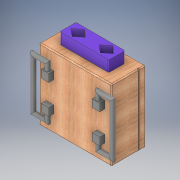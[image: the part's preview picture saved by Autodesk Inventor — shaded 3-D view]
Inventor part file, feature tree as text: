
AUTODESK INVENTOR PART (.ipt)
format: ipt  version: 2018 (Build 220112000, 112)  size: 627,200 bytes
history: native  units: in
note: dims shown in document units (in); Inventor stores cm internally (conversion verified against a paired STEP export)
features: extrude x16, sketch x16, projected_geometry x8, fillet x2
ambient origin geometry x8: Origin, YZ Plane, XZ Plane, XY Plane, X Axis, Y Axis, Z Axis, Center Point
bodies: Solid1 (feature_tree)
feature tree (42):
  extrude  "Extrusion1"  Depth=3.175in
  extrude  "Extrusion2"  Depth=1.517in TaperAngle=0.0deg
  fillet  "Fillet1"  Radius=3.175in
  extrude  "Extrusion3"  Depth=3.23in
  extrude  "Extrusion4"  Depth=0.8225in
  extrude  "Extrusion5"  Depth=0.05in
  extrude  "Extrusion6"  Depth=0.05in
  extrude  "Extrusion7"  Depth=0.31in
  extrude  "Extrusion8"  Depth=0.31in
  fillet  "Fillet2"  Radius=0.76in
  extrude  "Extrusion9"  Depth=0.76in
  extrude  "Extrusion10"  Depth=0.34in
  extrude  "Extrusion11"  Depth=0.34in
  extrude  "Extrusion12"  Depth=0.34in
  extrude  "Extrusion13"  Depth=0.0975in
  extrude  "Extrusion14"  Depth=0.0975in
  extrude  "Extrusion15"  Depth=0.0975in
  extrude  "Extrusion16"  Depth=1.155in
  sketch  "Sketch1"  dims[d0=3.23in d1=3.175in]
  sketch  "Sketch2"  dims[d2=0.05in d3=1.517in d4=0.0in d5=3.175in]
  sketch  "Sketch3"  dims[d8=3.23in d9=0.695in]
  sketch  "Sketch4"  dims[d10=0.8225in d11=0.8225in]
  sketch  "Sketch5"  dims[d12=0.695in d13=0.05in]
  projected_geometry  "Projected Loop1"
  projected_geometry  "Projected Loop2"
  sketch  "Sketch6"  dims[d14=1.155in d15=0.0in d16=0.05in]
  sketch  "Sketch7"  dims[d26=0.31in d27=0.31in]
  projected_geometry  "Projected Loop3"
  projected_geometry  "Projected Loop4"
  sketch  "Sketch8"  dims[d28=0.31in d29=0.31in d30=0.76in]
  sketch  "Sketch9"  dims[d31=0.76in d32=0.76in]
  sketch  "Sketch10"  dims[d33=0.76in d34=0.34in]
  sketch  "Sketch11"  dims[d35=0.34in d36=0.34in]
  sketch  "Sketch12"  dims[d37=0.34in d38=0.34in]
  projected_geometry  "Projected Loop5"
  projected_geometry  "Projected Loop6"
  projected_geometry  "Projected Loop7"
  sketch  "Sketch13"  dims[d39=0.215in d40=0.0in d42=0.0975in]
  sketch  "Sketch14"  dims[d43=0.0975in d44=0.195in]
  sketch  "Sketch15"  dims[d45=0.195in d46=0.0975in]
  projected_geometry  "Projected Loop8"
  sketch  "Sketch16"  dims[d47=0.0975in d48=0.195in d49=0.195in d50=0.3975in d51=0.0in d52=0.3975in d53=0.0in d54=0.195in d55=0.195in d56=0.63in d57=0.0in d58=0.63in d59=0.0in d60=0.195in d61=0.195in d62=0.195in d63=0.195in d64=0.63in d65=0.0in d66=0.0975in d67=0.4in d68=0.39in d69=0.39in d70=0.55in d71=0.4in d72=0.39in d73=0.4in d74=0.39in d75=0.59in d76=0.59in d77=0.59in d78=0.59in d79=0.305in d80=0.0in d81=0.395in d82=0.52in d83=0.52in d84=0.395in d85=0.05in d86=0.495in d87=0.0in d88=0.3635in d89=0.727in d90=0.14in d91=0.65in d92=0.325in d93=0.095in d94=0.095in d95=0.14in d96=0.65in d97=0.325in d98=0.495in d99=0.0in d100=0.495in d101=0.0in d102=0.267in d103=0.07in d104=0.05in d105=0.0in d106=0.05in d107=0.0in d108=0.52in d109=0.52in d110=0.395in d111=0.395in d112=0.005in d113=0.005in d114=0.005in d115=0.005in d116=0.005in d117=0.005in d118=0.005in d119=0.005in d120=0.005in d121=0.005in d122=0.005in d123=0.005in d124=0.005in d125=0.005in d126=0.005in d127=0.005in d128=0.005in d129=0.005in d130=0.005in d131=0.005in d132=0.005in d133=0.005in d134=0.005in d135=0.005in d136=180.0deg d137=180.0deg d138=180.0deg d139=180.0deg d140=0.0in d141=180.0deg d142=0.0in d143=0.05in d144=0.05in d145=0.05in d146=0.495in d147=0.0in d148=0.005in d149=0.005in d150=0.005in d151=0.005in d152=0.005in d153=0.005in d154=0.005in d155=0.005in d156=180.0deg d157=0.05in d158=0.05in d159=1.155in d160=0.0in]
